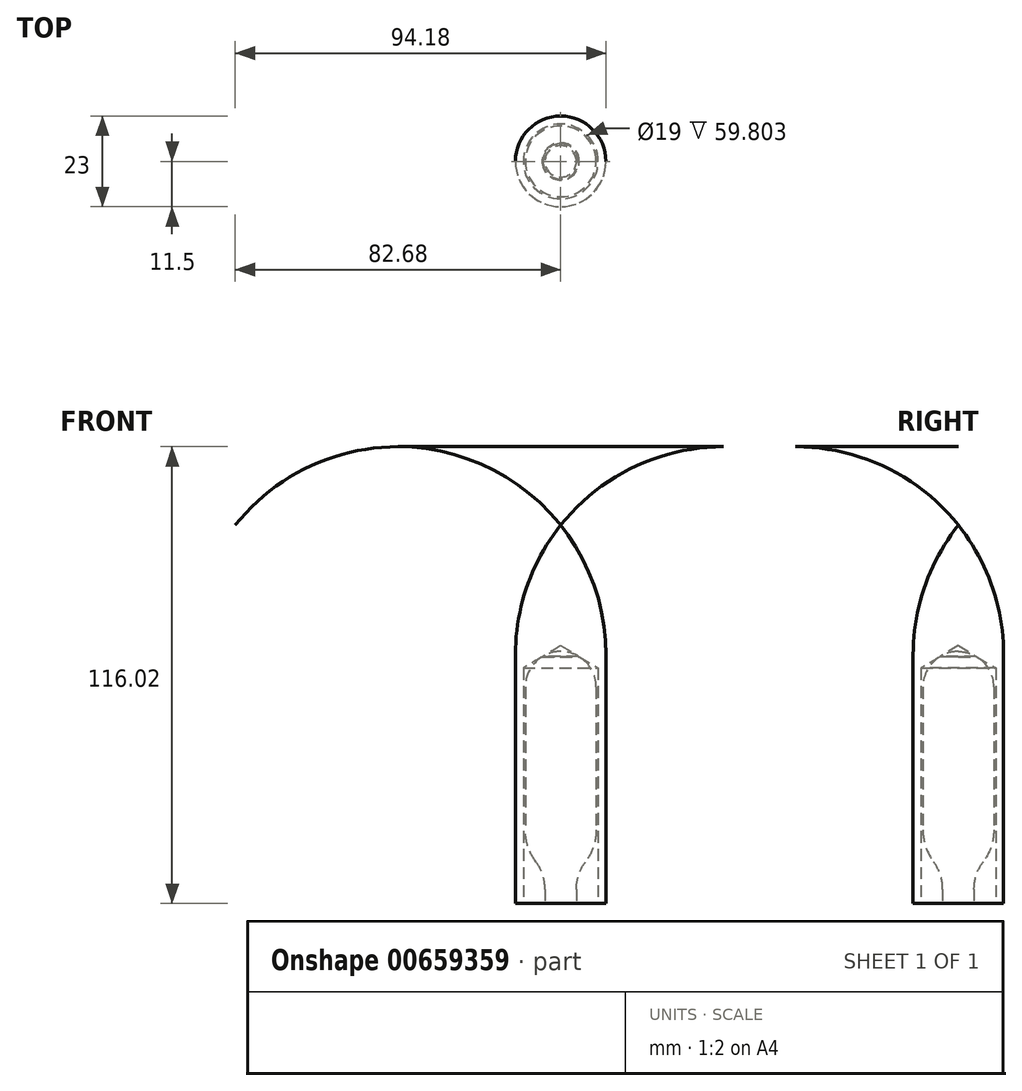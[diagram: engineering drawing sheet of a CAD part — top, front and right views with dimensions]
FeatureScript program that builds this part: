
annotation { "Feature Type Name" : "Feature", "Feature Type Description" : "" }
export const myFeature = defineFeature(function(context is Context, id is Id, definition is map)
    precondition{}
    {
        {
            var Q0;
            Q0=qCreatedBy(makeId("Right.planeOp"),FACE);
            var sketch = newSketch(context, id + "F0", { "sketchPlane" : qUnion([Q0])});
            skLineSegment(sketch, "E0", {"start": v(0, 0) * mm, "end": v(0, 64) * mm});
            skArc(sketch, "E1", {"start": v(9, 55) * mm, "mid": v(6.36, 61.36) * mm, "end": v(0, 64) * mm});
            skLineSegment(sketch, "E2", {"start": v(9, 55) * mm, "end": v(9, 18.64) * mm});
            skArc(sketch, "E3", {"start": v(6.32, 10.58) * mm, "mid": v(8.31, 14.4) * mm, "end": v(9, 18.64) * mm});
            skArc(sketch, "E4", {"start": v(6.32, 10.58) * mm, "mid": v(4.6, 7.28) * mm, "end": v(4, 3.6) * mm});
            skLineSegment(sketch, "E5", {"start": v(4, 3.6) * mm, "end": v(4, 0) * mm});
            skLineSegment(sketch, "E6", {"start": v(4, 0) * mm, "end": v(0, 0) * mm});
            skSolve(sketch);
        }
        {
            var Q0;
            Q0=makeQuery(id+"F0.imprint","IMPRINT",FACE,{"disambiguationData":[TD([[makeQuery(id+"F0.imprint","IMPRINT",EDGE,{"derivedFrom":sQuery(id+"F0.wireOp",EDGE,"E0")}),-1.0]])]});
            var Q1;
            Q1=sQuery(id+"F0.wireOp",EDGE,"E0");
            revolve(context, id + "F1", {"entities" : qUnion([Q0]), "axis" : qUnion([Q1]), "revolveType" : RevolveType.FULL});
        }
        {
            var Q0;
            Q0=qCreatedBy(makeId("Right.planeOp"),FACE);
            var sketch = newSketch(context, id + "F2", { "sketchPlane" : qUnion([Q0])});
            skLineSegment(sketch, "E7", {"start": v(0, 0) * mm, "end": v(0, 96.09) * mm});
            skLineSegment(sketch, "E8", {"start": v(0, 65.49) * mm, "end": v(9.5, 59.8) * mm});
            skLineSegment(sketch, "E9", {"start": v(9.5, 59.8) * mm, "end": v(9.5, 0) * mm});
            skLineSegment(sketch, "E10", {"start": v(9.5, 0) * mm, "end": v(11.5, 0) * mm});
            skLineSegment(sketch, "E11", {"start": v(11.5, 0) * mm, "end": v(11.5, 63.18) * mm});
            skArc(sketch, "E12", {"start": v(11.5, 63.18) * mm, "mid": v(8.54, 80.6) * mm, "end": v(0, 96.09) * mm});
            skSolve(sketch);
        }
        {
            var Q0;
            {var subQ0=sQuery(id+"F2.wireOp",EDGE,"E8");Q0=makeQuery(id+"F2.imprint","IMPRINT",FACE,{"disambiguationData":[TD([[makeQuery(id+"F2.imprint","IMPRINT",EDGE,{"derivedFrom":subQ0}),1.0]])]});}
            var Q1;
            Q1=sQuery(id+"F2.wireOp",EDGE,"E7");
            revolve(context, id + "F3", {"operationType" : NewBodyOperationType.ADD, "entities" : qUnion([Q0]), "axis" : qUnion([Q1]), "revolveType" : RevolveType.FULL});
        }
    });
